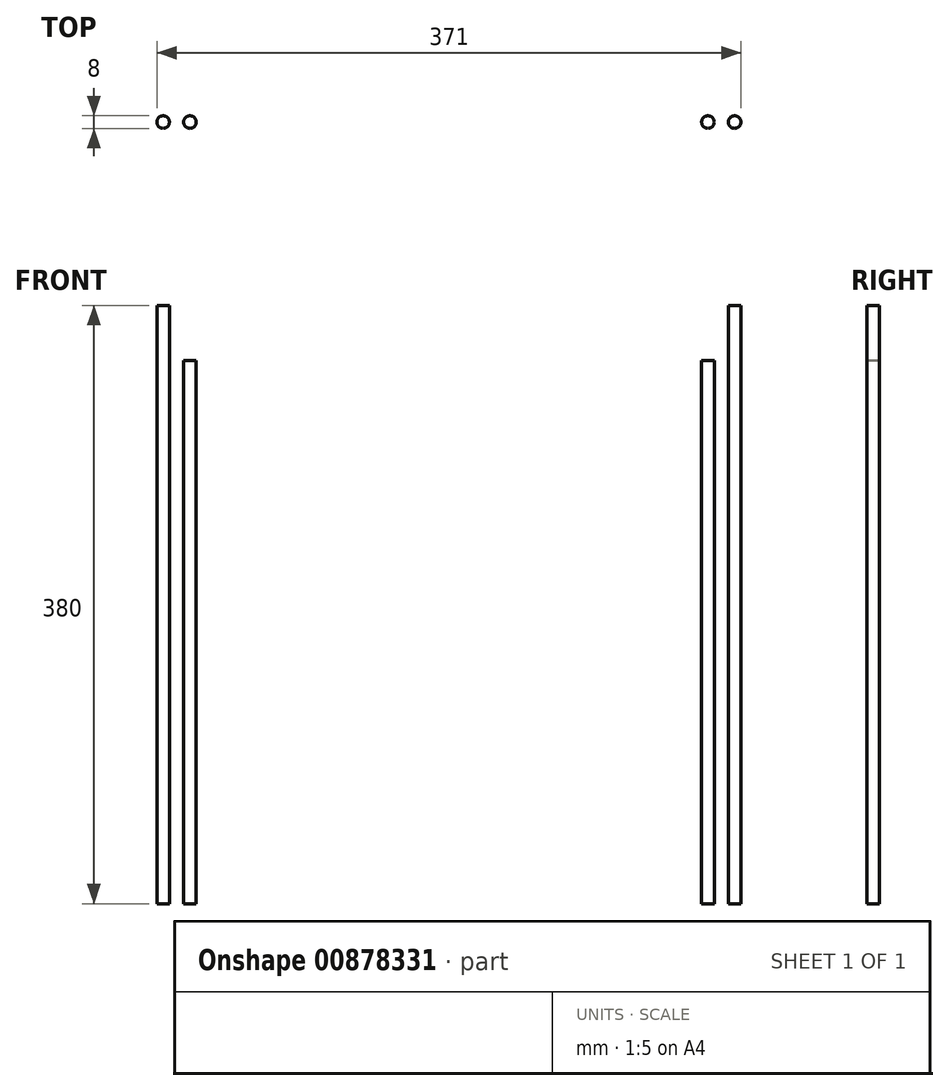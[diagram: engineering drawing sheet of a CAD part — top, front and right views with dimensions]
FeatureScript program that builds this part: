
annotation { "Feature Type Name" : "Feature", "Feature Type Description" : "" }
export const myFeature = defineFeature(function(context is Context, id is Id, definition is map)
    precondition{}
    {
        {
            var Q0;
            Q0=qCreatedBy(makeId("Top.planeOp"),FACE);
            var sketch = newSketch(context, id + "F0", { "sketchPlane" : qUnion([Q0])});
            skCircle(sketch, "E0", {"center": v(0, 0) * mm, "radius": 4 * mm});
            skCircle(sketch, "E1", {"center": v(17, 0) * mm, "radius": 4 * mm});
            skCircle(sketch, "E2", {"center": v(346, 0) * mm, "radius": 4 * mm});
            skCircle(sketch, "E3", {"center": v(363, 0) * mm, "radius": 4 * mm});
            skSolve(sketch);
        }
        {
            var Q0;
            Q0=makeQuery(id+"F0.imprint","IMPRINT",FACE,{"disambiguationData":[TD([[makeQuery(id+"F0.imprint","IMPRINT",EDGE,{"derivedFrom":sQuery(id+"F0.wireOp",EDGE,"E1")}),1.0]])]});
            var Q1;
            Q1=makeQuery(id+"F0.imprint","IMPRINT",FACE,{"disambiguationData":[TD([[makeQuery(id+"F0.imprint","IMPRINT",EDGE,{"derivedFrom":sQuery(id+"F0.wireOp",EDGE,"E0")}),1.0]])]});
            var Q2;
            Q2=makeQuery(id+"F0.imprint","IMPRINT",FACE,{"disambiguationData":[TD([[makeQuery(id+"F0.imprint","IMPRINT",EDGE,{"derivedFrom":sQuery(id+"F0.wireOp",EDGE,"E2")}),1.0]])]});
            var Q3;
            Q3=makeQuery(id+"F0.imprint","IMPRINT",FACE,{"disambiguationData":[TD([[makeQuery(id+"F0.imprint","IMPRINT",EDGE,{"derivedFrom":sQuery(id+"F0.wireOp",EDGE,"E3")}),1.0]])]});
            extrude(context, id + "F1", {"entities" : qUnion([Q0, Q1, Q2, Q3]), "depth" : 380 * mm, "offsetDistance" : 25 * mm});
        }
        {
            var Q0;
            Q0=makeQuery(id+"F1.opExtrude","CAP_FACE",FACE,{"disambiguationData":[OSD([sQuery(id+"F0.wireOp",EDGE,"E1")])],"isStart":false});
            extrude(context, id + "F2", {"entities" : qUnion([Q0]), "operationType" : NewBodyOperationType.REMOVE, "oppositeDirection" : true, "depth" : 35 * mm, "offsetDistance" : 25 * mm});
        }
        {
            var Q0;
            Q0=makeQuery(id+"F1.opExtrude","CAP_FACE",FACE,{"disambiguationData":[OSD([sQuery(id+"F0.wireOp",EDGE,"E2")])],"isStart":false});
            extrude(context, id + "F3", {"entities" : qUnion([Q0]), "operationType" : NewBodyOperationType.REMOVE, "oppositeDirection" : true, "depth" : 35 * mm, "offsetDistance" : 25 * mm});
        }
    });
